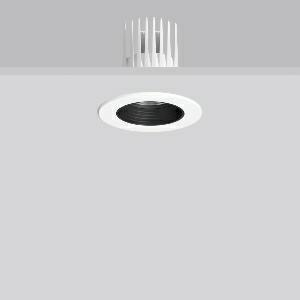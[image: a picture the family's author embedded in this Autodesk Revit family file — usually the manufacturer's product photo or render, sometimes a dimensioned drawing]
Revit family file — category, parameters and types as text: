
# Revit family: heledon_mini_e_901752_002_6767
name_source: partatom
category: Lighting Fixtures
units: mm (PartAtom-declared; Revit-internal decimal feet)

## family parameters
Cut with Voids When Loaded = No
Host = Face
Light Source = No
Part Type = Normal
Room Calculation Point = No
Round Connector Dimension = Use Diameter
Shared = No

## types (1)
- HELEDON mini E (1 x LED Modul 930, 3000 lm, 3000)
    Apparent Load = 29 VA
    Approval mark = CE
    CIE Flux Codes = 96 100 100 100 100
    Color Rendering = 90
    Color Temperature = 3000
    Default Elevation = 1800 mm
    Description = Series: HELEDON mini
Round recessed downlight. Housing: die-cast aluminium, powder-coated. Black plastic ring and recessed LED to prevent glare from the side. Optical assembly with lens made of plastic (polycarbonate) for the best homogeneous light distribution - can be changed without tools. Best colour rendering index Ra>90. Suitable for Recessed ceiling mounting. Installation without tools thanks to spring fastening system. Including separate LED converter with connecting cable 600 mm.High quality converter without flickering and stroboscopic effect. Through-wiring box (5 pole) available as accessory. The following accessories can be mounted without use of tools: interchangeable lenses, decorative glasses, honeycomb louvre, clear and frosted diffusers, white interchangeable plastic ring. 
Colour: traffic white, matt (RAL 9016)
Diameter: 124 mm
Height: 3 mm
Cut-out diameter: 114 mm
Recess height: 170 mm
Luminaire: recess height: 120 mm
Lamp: LED
Socket: without socket
Colour temperature: 3000K
Colour rendering index (CRI): 92
System power: 29 W
Rated luminous flux: 3000 lm
Luminous efficiency: 103 lm/W
Control gear: Regulated power supply
Protection class: II
Type of protection: IP 20
    Height = 0 mm  [stored 0 ft]
    Lamp = 1 x LED Modul 930
    Lamp Light Flux = 3000 lm
    Lamp count = 1
    Length = 124 mm  [stored 0.406824 ft]
    Lifetime = 50000 h
    Luminous efficacy = 103 lm/W
    Manufacturer = RZB
    ModVariant = No
    Model = 901752.002
    Mounting Place = Ceiling
    Mounting Type = Recessed
    Number of Poles = 1
    OnlyDefault = Yes
    Power Factor = 1
    Product Name = HELEDON mini E
    Product group = Recessed downlights
    ProductGroupID = 402
    Protection Class = Protection class II
    Protection Degree = IP 20
    RLX_Detail_Level = 1
    RLX_Emergency_Light_Flux = 0 lm
    RLX_Emergency_Type = 0
    RLX_Emergency_Type_DB = No
    RlxData = <blob elided: 125701 chars, md5=8879f513>
    Socket = socket
    Standby Power = 0 W
    System Light Flux = 3000 lm
    System Power = 29 W
    Type Comments = Product without accessories
    Type Image = 901656.002.jpg
    URL = http://relux.com
    VarID = ---
    Voltage = 230 V
    Voltage Range = 220-240 V
    Weight = 0.00 kg
    Width = 0 mm  [stored 0 ft]

note: [stored X ft] marks values corroborated as IEEE doubles in the binary element streams (Revit-internal decimal feet)

## geometry (parser evidence)
native form markers: Blend x4, Sweep x9
no freeform markers — native parametric forms only
